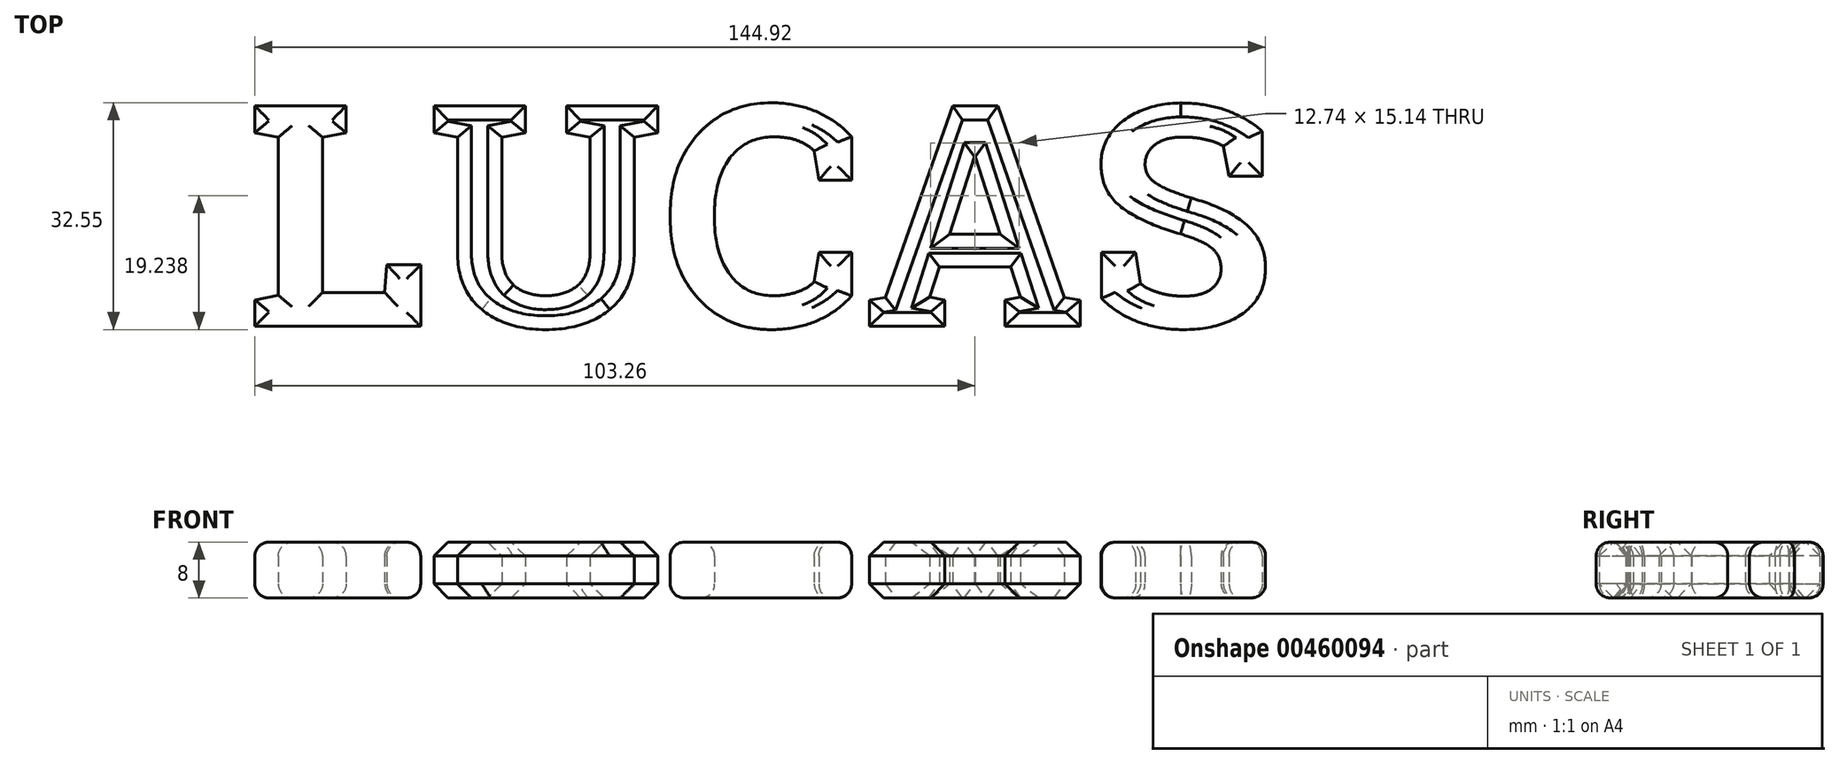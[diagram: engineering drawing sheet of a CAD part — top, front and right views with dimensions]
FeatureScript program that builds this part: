
annotation { "Feature Type Name" : "Feature", "Feature Type Description" : "" }
export const myFeature = defineFeature(function(context is Context, id is Id, definition is map)
    precondition{}
    {
        {
            var Q0;
            Q0=qCreatedBy(makeId("Top.planeOp"),FACE);
            var sketch = newSketch(context, id + "F0", { "sketchPlane" : qUnion([Q0])});
            skText(sketch, "E0", { "text": "LUCAS", "fontName": "RobotoSlab-Bold.ttf"});
            const initialGuessF0  = {"E0": [-0.07444, 0, 1, 0, 0.03203]};
            skSetInitialGuess(sketch, initialGuessF0);
            skSolve(sketch);
        }
        {
            var Q0;
            Q0 = qSketchRegion(id + "F0", true);
            extrude(context, id + "F1", {"entities" : qUnion([Q0]), "depth" : 8 * mm, "offsetDistance" : 25 * mm});
        }
        {
            var Q0;
            Q0=makeQuery(id+"F1.opExtrude","CAP_FACE",FACE,{"disambiguationData":[OSD([sQuery(id+"F0.wireOp",EDGE,"E0.sketch_text.stroke-0"),sQuery(id+"F0.wireOp",EDGE,"E0.sketch_text.stroke-1"),sQuery(id+"F0.wireOp",EDGE,"E0.sketch_text.stroke-2"),sQuery(id+"F0.wireOp",EDGE,"E0.sketch_text.stroke-3"),sQuery(id+"F0.wireOp",EDGE,"E0.sketch_text.stroke-4"),sQuery(id+"F0.wireOp",EDGE,"E0.sketch_text.stroke-5"),sQuery(id+"F0.wireOp",EDGE,"E0.sketch_text.stroke-6"),sQuery(id+"F0.wireOp",EDGE,"E0.sketch_text.stroke-7"),sQuery(id+"F0.wireOp",EDGE,"E0.sketch_text.stroke-8"),sQuery(id+"F0.wireOp",EDGE,"E0.sketch_text.stroke-9"),sQuery(id+"F0.wireOp",EDGE,"E0.sketch_text.stroke-10"),sQuery(id+"F0.wireOp",EDGE,"E0.sketch_text.stroke-11"),sQuery(id+"F0.wireOp",EDGE,"E0.sketch_text.stroke-12"),sQuery(id+"F0.wireOp",EDGE,"E0.sketch_text.stroke-13"),sQuery(id+"F0.wireOp",EDGE,"E0.sketch_text.stroke-14"),sQuery(id+"F0.wireOp",EDGE,"E0.sketch_text.stroke-15")])],"isStart":false});
            var Q1;
            Q1=makeQuery(id+"F1.opExtrude","CAP_FACE",FACE,{"disambiguationData":[OSD([sQuery(id+"F0.wireOp",EDGE,"E0.sketch_text.stroke-0"),sQuery(id+"F0.wireOp",EDGE,"E0.sketch_text.stroke-1"),sQuery(id+"F0.wireOp",EDGE,"E0.sketch_text.stroke-2"),sQuery(id+"F0.wireOp",EDGE,"E0.sketch_text.stroke-3"),sQuery(id+"F0.wireOp",EDGE,"E0.sketch_text.stroke-4"),sQuery(id+"F0.wireOp",EDGE,"E0.sketch_text.stroke-5"),sQuery(id+"F0.wireOp",EDGE,"E0.sketch_text.stroke-6"),sQuery(id+"F0.wireOp",EDGE,"E0.sketch_text.stroke-7"),sQuery(id+"F0.wireOp",EDGE,"E0.sketch_text.stroke-8"),sQuery(id+"F0.wireOp",EDGE,"E0.sketch_text.stroke-9"),sQuery(id+"F0.wireOp",EDGE,"E0.sketch_text.stroke-10"),sQuery(id+"F0.wireOp",EDGE,"E0.sketch_text.stroke-11"),sQuery(id+"F0.wireOp",EDGE,"E0.sketch_text.stroke-12"),sQuery(id+"F0.wireOp",EDGE,"E0.sketch_text.stroke-13"),sQuery(id+"F0.wireOp",EDGE,"E0.sketch_text.stroke-14"),sQuery(id+"F0.wireOp",EDGE,"E0.sketch_text.stroke-15")])],"isStart":true});
            var Q2;
            Q2=makeQuery(id+"F1.opExtrude","CAP_FACE",FACE,{"disambiguationData":[OSD([sQuery(id+"F0.wireOp",EDGE,"E0.sketch_text.stroke-40"),sQuery(id+"F0.wireOp",EDGE,"E0.sketch_text.stroke-41"),sQuery(id+"F0.wireOp",EDGE,"E0.sketch_text.stroke-42"),sQuery(id+"F0.wireOp",EDGE,"E0.sketch_text.stroke-43"),sQuery(id+"F0.wireOp",EDGE,"E0.sketch_text.stroke-44"),sQuery(id+"F0.wireOp",EDGE,"E0.sketch_text.stroke-45"),sQuery(id+"F0.wireOp",EDGE,"E0.sketch_text.stroke-46"),sQuery(id+"F0.wireOp",EDGE,"E0.sketch_text.stroke-47"),sQuery(id+"F0.wireOp",EDGE,"E0.sketch_text.stroke-48"),sQuery(id+"F0.wireOp",EDGE,"E0.sketch_text.stroke-49"),sQuery(id+"F0.wireOp",EDGE,"E0.sketch_text.stroke-50"),sQuery(id+"F0.wireOp",EDGE,"E0.sketch_text.stroke-51"),sQuery(id+"F0.wireOp",EDGE,"E0.sketch_text.stroke-52"),sQuery(id+"F0.wireOp",EDGE,"E0.sketch_text.stroke-53"),sQuery(id+"F0.wireOp",EDGE,"E0.sketch_text.stroke-54"),sQuery(id+"F0.wireOp",EDGE,"E0.sketch_text.stroke-55"),sQuery(id+"F0.wireOp",EDGE,"E0.sketch_text.stroke-56"),sQuery(id+"F0.wireOp",EDGE,"E0.sketch_text.stroke-57"),sQuery(id+"F0.wireOp",EDGE,"E0.sketch_text.stroke-58"),sQuery(id+"F0.wireOp",EDGE,"E0.sketch_text.stroke-59"),sQuery(id+"F0.wireOp",EDGE,"E0.sketch_text.stroke-60"),sQuery(id+"F0.wireOp",EDGE,"E0.sketch_text.stroke-61"),sQuery(id+"F0.wireOp",EDGE,"E0.sketch_text.stroke-62"),sQuery(id+"F0.wireOp",EDGE,"E0.sketch_text.stroke-63")])],"isStart":false});
            var Q3;
            Q3=makeQuery(id+"F1.opExtrude","CAP_FACE",FACE,{"disambiguationData":[OSD([sQuery(id+"F0.wireOp",EDGE,"E0.sketch_text.stroke-84"),sQuery(id+"F0.wireOp",EDGE,"E0.sketch_text.stroke-85"),sQuery(id+"F0.wireOp",EDGE,"E0.sketch_text.stroke-86"),sQuery(id+"F0.wireOp",EDGE,"E0.sketch_text.stroke-87"),sQuery(id+"F0.wireOp",EDGE,"E0.sketch_text.stroke-88"),sQuery(id+"F0.wireOp",EDGE,"E0.sketch_text.stroke-89"),sQuery(id+"F0.wireOp",EDGE,"E0.sketch_text.stroke-90"),sQuery(id+"F0.wireOp",EDGE,"E0.sketch_text.stroke-91"),sQuery(id+"F0.wireOp",EDGE,"E0.sketch_text.stroke-92"),sQuery(id+"F0.wireOp",EDGE,"E0.sketch_text.stroke-93"),sQuery(id+"F0.wireOp",EDGE,"E0.sketch_text.stroke-94"),sQuery(id+"F0.wireOp",EDGE,"E0.sketch_text.stroke-95"),sQuery(id+"F0.wireOp",EDGE,"E0.sketch_text.stroke-96"),sQuery(id+"F0.wireOp",EDGE,"E0.sketch_text.stroke-97"),sQuery(id+"F0.wireOp",EDGE,"E0.sketch_text.stroke-98"),sQuery(id+"F0.wireOp",EDGE,"E0.sketch_text.stroke-99"),sQuery(id+"F0.wireOp",EDGE,"E0.sketch_text.stroke-100"),sQuery(id+"F0.wireOp",EDGE,"E0.sketch_text.stroke-101"),sQuery(id+"F0.wireOp",EDGE,"E0.sketch_text.stroke-102"),sQuery(id+"F0.wireOp",EDGE,"E0.sketch_text.stroke-103"),sQuery(id+"F0.wireOp",EDGE,"E0.sketch_text.stroke-104"),sQuery(id+"F0.wireOp",EDGE,"E0.sketch_text.stroke-105"),sQuery(id+"F0.wireOp",EDGE,"E0.sketch_text.stroke-106"),sQuery(id+"F0.wireOp",EDGE,"E0.sketch_text.stroke-107"),sQuery(id+"F0.wireOp",EDGE,"E0.sketch_text.stroke-108"),sQuery(id+"F0.wireOp",EDGE,"E0.sketch_text.stroke-109"),sQuery(id+"F0.wireOp",EDGE,"E0.sketch_text.stroke-110"),sQuery(id+"F0.wireOp",EDGE,"E0.sketch_text.stroke-111"),sQuery(id+"F0.wireOp",EDGE,"E0.sketch_text.stroke-112"),sQuery(id+"F0.wireOp",EDGE,"E0.sketch_text.stroke-113")])],"isStart":false});
            var Q4;
            Q4=makeQuery(id+"F1.opExtrude","CAP_FACE",FACE,{"disambiguationData":[OSD([sQuery(id+"F0.wireOp",EDGE,"E0.sketch_text.stroke-84"),sQuery(id+"F0.wireOp",EDGE,"E0.sketch_text.stroke-85"),sQuery(id+"F0.wireOp",EDGE,"E0.sketch_text.stroke-86"),sQuery(id+"F0.wireOp",EDGE,"E0.sketch_text.stroke-87"),sQuery(id+"F0.wireOp",EDGE,"E0.sketch_text.stroke-88"),sQuery(id+"F0.wireOp",EDGE,"E0.sketch_text.stroke-89"),sQuery(id+"F0.wireOp",EDGE,"E0.sketch_text.stroke-90"),sQuery(id+"F0.wireOp",EDGE,"E0.sketch_text.stroke-91"),sQuery(id+"F0.wireOp",EDGE,"E0.sketch_text.stroke-92"),sQuery(id+"F0.wireOp",EDGE,"E0.sketch_text.stroke-93"),sQuery(id+"F0.wireOp",EDGE,"E0.sketch_text.stroke-94"),sQuery(id+"F0.wireOp",EDGE,"E0.sketch_text.stroke-95"),sQuery(id+"F0.wireOp",EDGE,"E0.sketch_text.stroke-96"),sQuery(id+"F0.wireOp",EDGE,"E0.sketch_text.stroke-97"),sQuery(id+"F0.wireOp",EDGE,"E0.sketch_text.stroke-98"),sQuery(id+"F0.wireOp",EDGE,"E0.sketch_text.stroke-99"),sQuery(id+"F0.wireOp",EDGE,"E0.sketch_text.stroke-100"),sQuery(id+"F0.wireOp",EDGE,"E0.sketch_text.stroke-101"),sQuery(id+"F0.wireOp",EDGE,"E0.sketch_text.stroke-102"),sQuery(id+"F0.wireOp",EDGE,"E0.sketch_text.stroke-103"),sQuery(id+"F0.wireOp",EDGE,"E0.sketch_text.stroke-104"),sQuery(id+"F0.wireOp",EDGE,"E0.sketch_text.stroke-105"),sQuery(id+"F0.wireOp",EDGE,"E0.sketch_text.stroke-106"),sQuery(id+"F0.wireOp",EDGE,"E0.sketch_text.stroke-107"),sQuery(id+"F0.wireOp",EDGE,"E0.sketch_text.stroke-108"),sQuery(id+"F0.wireOp",EDGE,"E0.sketch_text.stroke-109"),sQuery(id+"F0.wireOp",EDGE,"E0.sketch_text.stroke-110"),sQuery(id+"F0.wireOp",EDGE,"E0.sketch_text.stroke-111"),sQuery(id+"F0.wireOp",EDGE,"E0.sketch_text.stroke-112"),sQuery(id+"F0.wireOp",EDGE,"E0.sketch_text.stroke-113")])],"isStart":true});
            var Q5;
            Q5=makeQuery(id+"F1.opExtrude","CAP_FACE",FACE,{"disambiguationData":[OSD([sQuery(id+"F0.wireOp",EDGE,"E0.sketch_text.stroke-40"),sQuery(id+"F0.wireOp",EDGE,"E0.sketch_text.stroke-41"),sQuery(id+"F0.wireOp",EDGE,"E0.sketch_text.stroke-42"),sQuery(id+"F0.wireOp",EDGE,"E0.sketch_text.stroke-43"),sQuery(id+"F0.wireOp",EDGE,"E0.sketch_text.stroke-44"),sQuery(id+"F0.wireOp",EDGE,"E0.sketch_text.stroke-45"),sQuery(id+"F0.wireOp",EDGE,"E0.sketch_text.stroke-46"),sQuery(id+"F0.wireOp",EDGE,"E0.sketch_text.stroke-47"),sQuery(id+"F0.wireOp",EDGE,"E0.sketch_text.stroke-48"),sQuery(id+"F0.wireOp",EDGE,"E0.sketch_text.stroke-49"),sQuery(id+"F0.wireOp",EDGE,"E0.sketch_text.stroke-50"),sQuery(id+"F0.wireOp",EDGE,"E0.sketch_text.stroke-51"),sQuery(id+"F0.wireOp",EDGE,"E0.sketch_text.stroke-52"),sQuery(id+"F0.wireOp",EDGE,"E0.sketch_text.stroke-53"),sQuery(id+"F0.wireOp",EDGE,"E0.sketch_text.stroke-54"),sQuery(id+"F0.wireOp",EDGE,"E0.sketch_text.stroke-55"),sQuery(id+"F0.wireOp",EDGE,"E0.sketch_text.stroke-56"),sQuery(id+"F0.wireOp",EDGE,"E0.sketch_text.stroke-57"),sQuery(id+"F0.wireOp",EDGE,"E0.sketch_text.stroke-58"),sQuery(id+"F0.wireOp",EDGE,"E0.sketch_text.stroke-59"),sQuery(id+"F0.wireOp",EDGE,"E0.sketch_text.stroke-60"),sQuery(id+"F0.wireOp",EDGE,"E0.sketch_text.stroke-61"),sQuery(id+"F0.wireOp",EDGE,"E0.sketch_text.stroke-62"),sQuery(id+"F0.wireOp",EDGE,"E0.sketch_text.stroke-63")])],"isStart":true});
            fillet(context, id + "F2", {"entities" : qUnion([Q0, Q1, Q2, Q3, Q4, Q5]), "tangentPropagation" : true, "radius" : 2 * mm, "defaultsChanged" : false, "vertexSettings" : [], "allowEdgeOverflow" : false});
        }
        {
            var Q0;
            Q0=makeQuery(id+"F1.opExtrude","CAP_FACE",FACE,{"disambiguationData":[OSD([sQuery(id+"F0.wireOp",EDGE,"E0.sketch_text.stroke-16"),sQuery(id+"F0.wireOp",EDGE,"E0.sketch_text.stroke-17"),sQuery(id+"F0.wireOp",EDGE,"E0.sketch_text.stroke-18"),sQuery(id+"F0.wireOp",EDGE,"E0.sketch_text.stroke-19"),sQuery(id+"F0.wireOp",EDGE,"E0.sketch_text.stroke-20"),sQuery(id+"F0.wireOp",EDGE,"E0.sketch_text.stroke-21"),sQuery(id+"F0.wireOp",EDGE,"E0.sketch_text.stroke-22"),sQuery(id+"F0.wireOp",EDGE,"E0.sketch_text.stroke-23"),sQuery(id+"F0.wireOp",EDGE,"E0.sketch_text.stroke-24"),sQuery(id+"F0.wireOp",EDGE,"E0.sketch_text.stroke-25"),sQuery(id+"F0.wireOp",EDGE,"E0.sketch_text.stroke-26"),sQuery(id+"F0.wireOp",EDGE,"E0.sketch_text.stroke-27"),sQuery(id+"F0.wireOp",EDGE,"E0.sketch_text.stroke-28"),sQuery(id+"F0.wireOp",EDGE,"E0.sketch_text.stroke-29"),sQuery(id+"F0.wireOp",EDGE,"E0.sketch_text.stroke-30"),sQuery(id+"F0.wireOp",EDGE,"E0.sketch_text.stroke-31"),sQuery(id+"F0.wireOp",EDGE,"E0.sketch_text.stroke-32"),sQuery(id+"F0.wireOp",EDGE,"E0.sketch_text.stroke-33"),sQuery(id+"F0.wireOp",EDGE,"E0.sketch_text.stroke-34"),sQuery(id+"F0.wireOp",EDGE,"E0.sketch_text.stroke-35"),sQuery(id+"F0.wireOp",EDGE,"E0.sketch_text.stroke-36"),sQuery(id+"F0.wireOp",EDGE,"E0.sketch_text.stroke-37"),sQuery(id+"F0.wireOp",EDGE,"E0.sketch_text.stroke-38"),sQuery(id+"F0.wireOp",EDGE,"E0.sketch_text.stroke-39")])],"isStart":false});
            var Q1;
            Q1=makeQuery(id+"F1.opExtrude","CAP_FACE",FACE,{"disambiguationData":[OSD([sQuery(id+"F0.wireOp",EDGE,"E0.sketch_text.stroke-64"),sQuery(id+"F0.wireOp",EDGE,"E0.sketch_text.stroke-65"),sQuery(id+"F0.wireOp",EDGE,"E0.sketch_text.stroke-66"),sQuery(id+"F0.wireOp",EDGE,"E0.sketch_text.stroke-67"),sQuery(id+"F0.wireOp",EDGE,"E0.sketch_text.stroke-68"),sQuery(id+"F0.wireOp",EDGE,"E0.sketch_text.stroke-69"),sQuery(id+"F0.wireOp",EDGE,"E0.sketch_text.stroke-70"),sQuery(id+"F0.wireOp",EDGE,"E0.sketch_text.stroke-71"),sQuery(id+"F0.wireOp",EDGE,"E0.sketch_text.stroke-72"),sQuery(id+"F0.wireOp",EDGE,"E0.sketch_text.stroke-73"),sQuery(id+"F0.wireOp",EDGE,"E0.sketch_text.stroke-74"),sQuery(id+"F0.wireOp",EDGE,"E0.sketch_text.stroke-75"),sQuery(id+"F0.wireOp",EDGE,"E0.sketch_text.stroke-76"),sQuery(id+"F0.wireOp",EDGE,"E0.sketch_text.stroke-77"),sQuery(id+"F0.wireOp",EDGE,"E0.sketch_text.stroke-78"),sQuery(id+"F0.wireOp",EDGE,"E0.sketch_text.stroke-79"),sQuery(id+"F0.wireOp",EDGE,"E0.sketch_text.stroke-80"),sQuery(id+"F0.wireOp",EDGE,"E0.sketch_text.stroke-81"),sQuery(id+"F0.wireOp",EDGE,"E0.sketch_text.stroke-82"),sQuery(id+"F0.wireOp",EDGE,"E0.sketch_text.stroke-83")])],"isStart":false});
            var Q2;
            Q2=makeQuery(id+"F1.opExtrude","CAP_FACE",FACE,{"disambiguationData":[OSD([sQuery(id+"F0.wireOp",EDGE,"E0.sketch_text.stroke-64"),sQuery(id+"F0.wireOp",EDGE,"E0.sketch_text.stroke-65"),sQuery(id+"F0.wireOp",EDGE,"E0.sketch_text.stroke-66"),sQuery(id+"F0.wireOp",EDGE,"E0.sketch_text.stroke-67"),sQuery(id+"F0.wireOp",EDGE,"E0.sketch_text.stroke-68"),sQuery(id+"F0.wireOp",EDGE,"E0.sketch_text.stroke-69"),sQuery(id+"F0.wireOp",EDGE,"E0.sketch_text.stroke-70"),sQuery(id+"F0.wireOp",EDGE,"E0.sketch_text.stroke-71"),sQuery(id+"F0.wireOp",EDGE,"E0.sketch_text.stroke-72"),sQuery(id+"F0.wireOp",EDGE,"E0.sketch_text.stroke-73"),sQuery(id+"F0.wireOp",EDGE,"E0.sketch_text.stroke-74"),sQuery(id+"F0.wireOp",EDGE,"E0.sketch_text.stroke-75"),sQuery(id+"F0.wireOp",EDGE,"E0.sketch_text.stroke-76"),sQuery(id+"F0.wireOp",EDGE,"E0.sketch_text.stroke-77"),sQuery(id+"F0.wireOp",EDGE,"E0.sketch_text.stroke-78"),sQuery(id+"F0.wireOp",EDGE,"E0.sketch_text.stroke-79"),sQuery(id+"F0.wireOp",EDGE,"E0.sketch_text.stroke-80"),sQuery(id+"F0.wireOp",EDGE,"E0.sketch_text.stroke-81"),sQuery(id+"F0.wireOp",EDGE,"E0.sketch_text.stroke-82"),sQuery(id+"F0.wireOp",EDGE,"E0.sketch_text.stroke-83")])],"isStart":true});
            var Q3;
            Q3=makeQuery(id+"F1.opExtrude","CAP_FACE",FACE,{"disambiguationData":[OSD([sQuery(id+"F0.wireOp",EDGE,"E0.sketch_text.stroke-16"),sQuery(id+"F0.wireOp",EDGE,"E0.sketch_text.stroke-17"),sQuery(id+"F0.wireOp",EDGE,"E0.sketch_text.stroke-18"),sQuery(id+"F0.wireOp",EDGE,"E0.sketch_text.stroke-19"),sQuery(id+"F0.wireOp",EDGE,"E0.sketch_text.stroke-20"),sQuery(id+"F0.wireOp",EDGE,"E0.sketch_text.stroke-21"),sQuery(id+"F0.wireOp",EDGE,"E0.sketch_text.stroke-22"),sQuery(id+"F0.wireOp",EDGE,"E0.sketch_text.stroke-23"),sQuery(id+"F0.wireOp",EDGE,"E0.sketch_text.stroke-24"),sQuery(id+"F0.wireOp",EDGE,"E0.sketch_text.stroke-25"),sQuery(id+"F0.wireOp",EDGE,"E0.sketch_text.stroke-26"),sQuery(id+"F0.wireOp",EDGE,"E0.sketch_text.stroke-27"),sQuery(id+"F0.wireOp",EDGE,"E0.sketch_text.stroke-28"),sQuery(id+"F0.wireOp",EDGE,"E0.sketch_text.stroke-29"),sQuery(id+"F0.wireOp",EDGE,"E0.sketch_text.stroke-30"),sQuery(id+"F0.wireOp",EDGE,"E0.sketch_text.stroke-31"),sQuery(id+"F0.wireOp",EDGE,"E0.sketch_text.stroke-32"),sQuery(id+"F0.wireOp",EDGE,"E0.sketch_text.stroke-33"),sQuery(id+"F0.wireOp",EDGE,"E0.sketch_text.stroke-34"),sQuery(id+"F0.wireOp",EDGE,"E0.sketch_text.stroke-35"),sQuery(id+"F0.wireOp",EDGE,"E0.sketch_text.stroke-36"),sQuery(id+"F0.wireOp",EDGE,"E0.sketch_text.stroke-37"),sQuery(id+"F0.wireOp",EDGE,"E0.sketch_text.stroke-38"),sQuery(id+"F0.wireOp",EDGE,"E0.sketch_text.stroke-39")])],"isStart":true});
            chamfer(context, id + "F3", {"entities" : qUnion([Q0, Q1, Q2, Q3]), "width" : 2 * mm, "tangentPropagation" : true});
        }
    });
